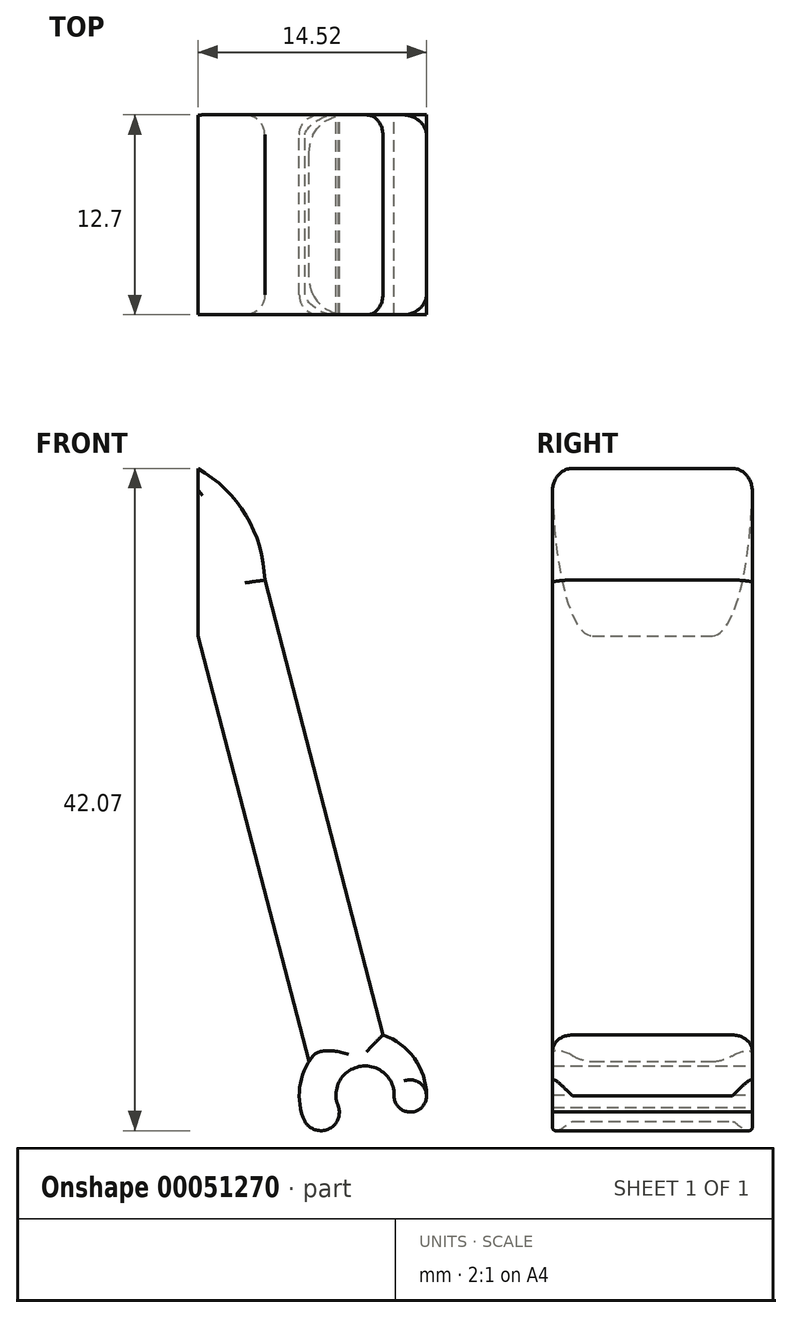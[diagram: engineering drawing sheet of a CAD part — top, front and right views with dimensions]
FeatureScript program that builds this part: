
annotation { "Feature Type Name" : "Feature", "Feature Type Description" : "" }
export const myFeature = defineFeature(function(context is Context, id is Id, definition is map)
    precondition{}
    {
        {
            var Q0;
            Q0=qCreatedBy(makeId("Front.planeOp"),FACE);
            var sketch = newSketch(context, id + "F0", { "sketchPlane" : qUnion([Q0])});
            skLineSegment(sketch, "E0", {"start": v(0, 31.94) * mm, "end": v(7.07, 4.91) * mm});
            skLineSegment(sketch, "E1", {"start": v(11.78, 6.5) * mm, "end": v(4.25, 35.48) * mm});
            skLineSegment(sketch, "E2", {"start": v(0, 42.58) * mm, "end": v(0, 31.94) * mm});
            skArc(sketch, "E3", {"start": v(4.25, 35.48) * mm, "mid": v(3.06, 39.59) * mm, "end": v(0, 42.58) * mm});
            skPoint(sketch, "E4.orphan", {"position": v(7.02, 0) * mm});
            skPoint(sketch, "E5.orphan", {"position": v(15.08, 0) * mm});
            skArc(sketch, "E6", {"start": v(14.52, 2.73) * mm, "mid": v(13.76, 5.1) * mm, "end": v(11.75, 6.58) * mm});
            skArc(sketch, "E7", {"start": v(12.47, 2.77) * mm, "mid": v(10.23, 4.58) * mm, "end": v(8.94, 2) * mm});
            skArc(sketch, "E8", {"start": v(12.47, 2.77) * mm, "mid": v(13.47, 1.69) * mm, "end": v(14.52, 2.73) * mm});
            skArc(sketch, "E9", {"start": v(6.8, 1.1) * mm, "mid": v(8.27, 0.6) * mm, "end": v(8.94, 2) * mm});
            skArc(sketch, "E10.trimOffspring", {"start": v(7.07, 4.91) * mm, "mid": v(6.45, 3.04) * mm, "end": v(6.8, 1.1) * mm});
            skSolve(sketch);
        }
        {
            var Q0;
            Q0=makeQuery(id+"F0.imprint","IMPRINT",FACE,{"disambiguationData":[TD([[makeQuery(id+"F0.imprint","IMPRINT",EDGE,{"derivedFrom":sQuery(id+"F0.wireOp",EDGE,"E0")}),1.0]])]});
            extrude(context, id + "F1", {"entities" : qUnion([Q0]), "depth" : 12.7 * mm});
        }
        {
            var Q0;
            Q0=makeQuery(id+"F1.opExtrude","CAP_EDGE",EDGE,{"disambiguationData":[OSD([sQuery(id+"F0.wireOp",EDGE,"E0")])],"isStart":true});
            var Q1;
            Q1=makeQuery(id+"F1.opExtrude","CAP_EDGE",EDGE,{"disambiguationData":[OSD([sQuery(id+"F0.wireOp",EDGE,"E0")])],"isStart":false});
            fillet(context, id + "F2", {"entities" : qUnion([Q0, Q1]), "radius" : 2.54 * mm, "tangentPropagation" : true, "allowEdgeOverflow" : false});
        }
        {
            var Q0;
            Q0=makeQuery(id+"F1.opExtrude","CAP_EDGE",EDGE,{"disambiguationData":[OSD([sQuery(id+"F0.wireOp",EDGE,"E1")])],"isStart":false});
            var Q1;
            Q1=makeQuery(id+"F1.opExtrude","CAP_EDGE",EDGE,{"disambiguationData":[OSD([sQuery(id+"F0.wireOp",EDGE,"E1")])],"isStart":true});
            fillet(context, id + "F3", {"entities" : qUnion([Q0, Q1]), "radius" : 1.27 * mm, "tangentPropagation" : true, "allowEdgeOverflow" : false});
        }
        {
            var Q0;
            Q0=makeQuery(id+"F1.opExtrude","CAP_EDGE",EDGE,{"disambiguationData":[OSD([sQuery(id+"F0.wireOp",EDGE,"E3")])],"isStart":true});
            fillet(context, id + "F4", {"entities" : qUnion([Q0]), "radius" : 1.27 * mm, "tangentPropagation" : true, "allowEdgeOverflow" : false});
        }
        {
            var Q0;
            Q0=makeQuery(id+"F1.opExtrude","CAP_EDGE",EDGE,{"disambiguationData":[OSD([sQuery(id+"F0.wireOp",EDGE,"E3")])],"isStart":false});
            fillet(context, id + "F5", {"entities" : qUnion([Q0]), "radius" : 1.27 * mm, "tangentPropagation" : true, "allowEdgeOverflow" : false});
        }
        {
            var Q0;
            Q0=makeQuery(id+"F1.opExtrude","CAP_EDGE",EDGE,{"disambiguationData":[OSD([sQuery(id+"F0.wireOp",EDGE,"E6")])],"isStart":false});
            var Q1;
            Q1=makeQuery(id+"F1.opExtrude","CAP_EDGE",EDGE,{"disambiguationData":[OSD([sQuery(id+"F0.wireOp",EDGE,"E10.trimOffspring")])],"isStart":false});
            var Q2;
            Q2=makeQuery(id+"F1.opExtrude","CAP_EDGE",EDGE,{"disambiguationData":[OSD([sQuery(id+"F0.wireOp",EDGE,"E10.trimOffspring")])],"isStart":true});
            var Q3;
            Q3=makeQuery(id+"F1.opExtrude","CAP_EDGE",EDGE,{"disambiguationData":[OSD([sQuery(id+"F0.wireOp",EDGE,"E6")])],"isStart":true});
            fillet(context, id + "F6", {"entities" : qUnion([Q0, Q1, Q2, Q3]), "radius" : 1.27 * mm, "tangentPropagation" : true, "allowEdgeOverflow" : false});
        }
    });
